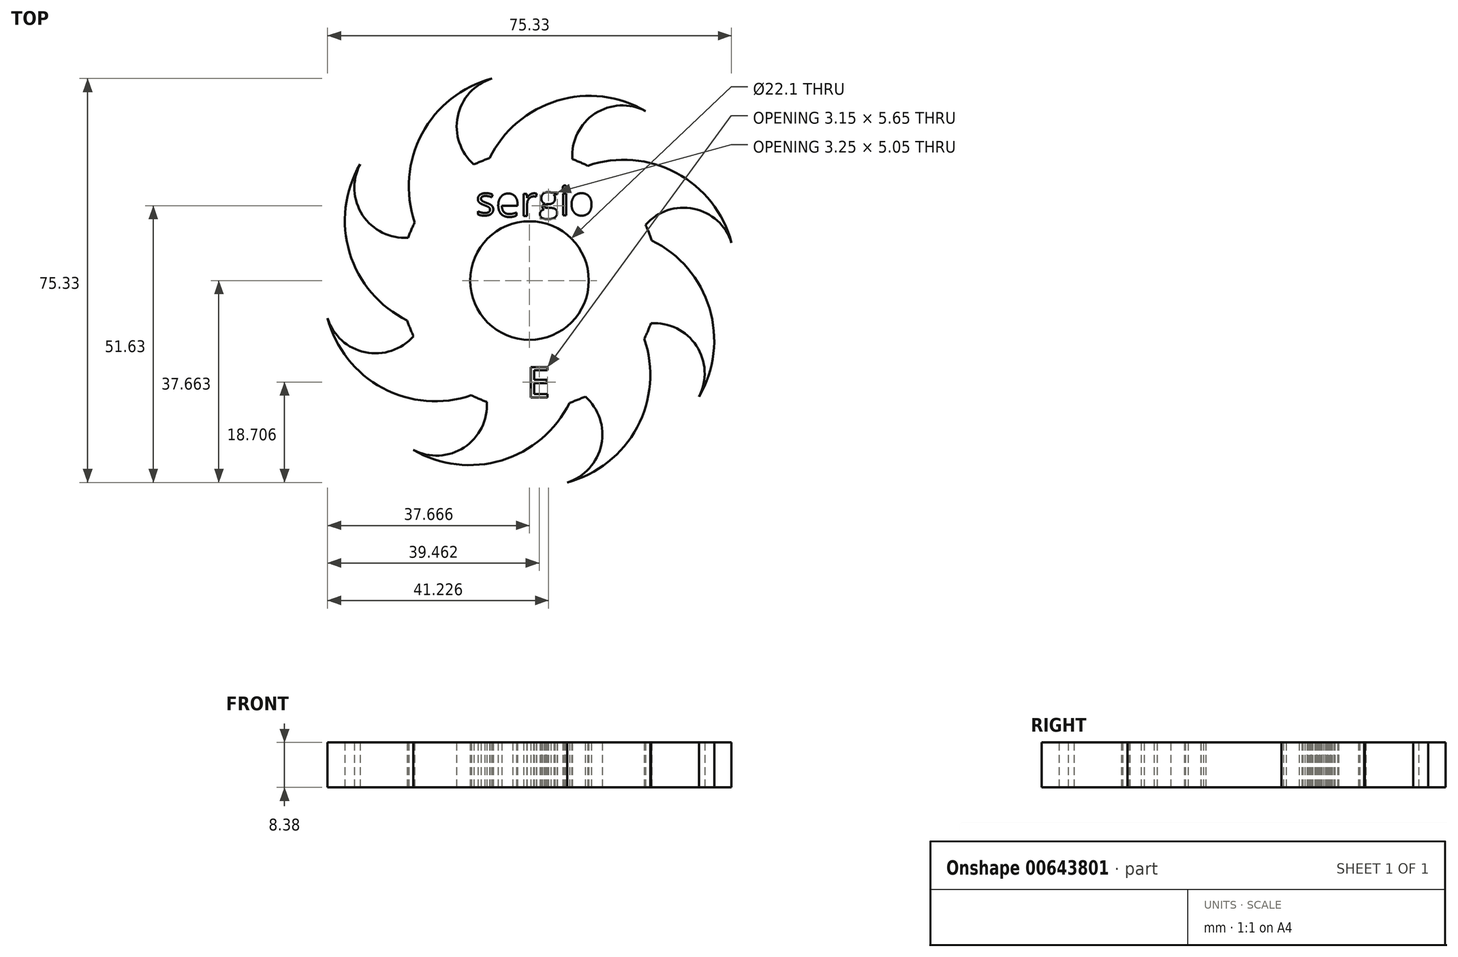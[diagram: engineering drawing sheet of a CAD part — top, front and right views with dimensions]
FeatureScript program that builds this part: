
annotation { "Feature Type Name" : "Feature", "Feature Type Description" : "" }
export const myFeature = defineFeature(function(context is Context, id is Id, definition is map)
    precondition{}
    {
        {
            var Q0;
            Q0=qCreatedBy(makeId("Top.planeOp"),FACE);
            var sketch = newSketch(context, id + "F0", { "sketchPlane" : qUnion([Q0])});
            skArc(sketch, "E0", {"start": v(-10.92, 50.97) * mm, "mid": v(-24.18, 40.22) * mm, "end": v(-24.92, 23.18) * mm});
            skArc(sketch, "E1", {"start": v(-10.92, 50.97) * mm, "mid": v(-17.27, 43.93) * mm, "end": v(-14.25, 34.94) * mm});
            skArc(sketch, "E2.1.0", {"start": v(-35.49, 34.96) * mm, "mid": v(-37.27, 18) * mm, "end": v(-25.74, 5.4) * mm});
            skArc(sketch, "E2.1.1", {"start": v(-35.49, 34.96) * mm, "mid": v(-35, 25.5) * mm, "end": v(-26.51, 21.28) * mm});
            skArc(sketch, "E2.2.0", {"start": v(-41.55, 6.27) * mm, "mid": v(-30.8, -6.99) * mm, "end": v(-13.76, -7.74) * mm});
            skArc(sketch, "E2.2.1", {"start": v(-41.55, 6.27) * mm, "mid": v(-34.5, -0.09) * mm, "end": v(-25.52, 2.94) * mm});
            skArc(sketch, "E2.3.0", {"start": v(-25.54, -18.3) * mm, "mid": v(-8.57, -20.08) * mm, "end": v(4.01, -8.55) * mm});
            skArc(sketch, "E2.3.1", {"start": v(-25.54, -18.3) * mm, "mid": v(-16.07, -17.82) * mm, "end": v(-11.86, -9.32) * mm});
            skArc(sketch, "E2.4.0", {"start": v(3.15, -24.36) * mm, "mid": v(16.4, -13.62) * mm, "end": v(17.15, 3.43) * mm});
            skArc(sketch, "E2.4.1", {"start": v(3.15, -24.36) * mm, "mid": v(9.5, -17.32) * mm, "end": v(6.48, -8.34) * mm});
            skArc(sketch, "E2.5.0", {"start": v(27.72, -8.36) * mm, "mid": v(29.5, 8.62) * mm, "end": v(17.97, 21.2) * mm});
            skArc(sketch, "E2.5.1", {"start": v(27.72, -8.36) * mm, "mid": v(27.24, 1.12) * mm, "end": v(18.74, 5.33) * mm});
            skArc(sketch, "E2.6.0", {"start": v(33.78, 20.34) * mm, "mid": v(23.04, 33.6) * mm, "end": v(5.99, 34.34) * mm});
            skArc(sketch, "E2.6.1", {"start": v(33.78, 20.34) * mm, "mid": v(26.74, 26.7) * mm, "end": v(17.75, 23.66) * mm});
            skArc(sketch, "E2.7.0", {"start": v(17.77, 44.9) * mm, "mid": v(0.8, 46.69) * mm, "end": v(-11.78, 35.16) * mm});
            skArc(sketch, "E2.7.1", {"start": v(17.77, 44.9) * mm, "mid": v(8.3, 44.43) * mm, "end": v(4.1, 35.93) * mm});
            skPoint(sketch, "E2.center", {"position": v(-3.88, 13.3) * mm});
            skArc(sketch, "E3", {"start": v(-11.34, 36.1) * mm, "mid": v(-12.81, 35.57) * mm, "end": v(-14.25, 34.94) * mm});
            skCircle(sketch, "E4", {"center": v(-3.88, 13.3) * mm, "radius": 11.05 * mm});
            skArc(sketch, "E5.trimOffspring", {"start": v(-25.28, 24.15) * mm, "mid": v(-25.94, 22.73) * mm, "end": v(-26.51, 21.28) * mm});
            skArc(sketch, "E6.trimOffspring", {"start": v(-26.69, 5.84) * mm, "mid": v(-26.15, 4.37) * mm, "end": v(-25.52, 2.94) * mm});
            skArc(sketch, "E7.trimOffspring", {"start": v(-14.73, -8.1) * mm, "mid": v(-13.32, -8.76) * mm, "end": v(-11.86, -9.32) * mm});
            skArc(sketch, "E8.trimOffspring", {"start": v(3.58, -9.5) * mm, "mid": v(5.05, -8.96) * mm, "end": v(6.48, -8.34) * mm});
            skArc(sketch, "E9.trimOffspring", {"start": v(17.51, 2.46) * mm, "mid": v(18.18, 3.87) * mm, "end": v(18.74, 5.33) * mm});
            skArc(sketch, "E10.trimOffspring", {"start": v(18.92, 20.76) * mm, "mid": v(18.38, 22.23) * mm, "end": v(17.75, 23.66) * mm});
            skArc(sketch, "E11.trimOffspring", {"start": v(6.96, 34.7) * mm, "mid": v(5.55, 35.36) * mm, "end": v(4.1, 35.93) * mm});
            skText(sketch, "E12", { "text": "s", "fontName": "OpenSans-Regular.ttf"});
            skText(sketch, "E13", { "text": "e", "fontName": "OpenSans-Regular.ttf"});
            skText(sketch, "E14", { "text": "r", "fontName": "OpenSans-Regular.ttf"});
            skText(sketch, "E15", { "text": "i", "fontName": "OpenSans-Regular.ttf"});
            skText(sketch, "E16", { "text": "o", "fontName": "OpenSans-Regular.ttf"});
            skText(sketch, "E17", { "text": "E", "fontName": "OpenSans-Regular.ttf"});
            skText(sketch, "E18", { "text": "g", "fontName": "OpenSans-Regular.ttf"});
            const initialGuessF0  = {"E12": [-0.01391, 0.02547, 1, 0, 0.00545], "E13": [-0.01016, 0.02522, 1, 0, 0.0057], "E14": [-0.00562, 0.02534, 1, 0, 0.00558], "E15": [0.00172, 0.02547, 1, 0, 0.00545], "E16": [0.00353, 0.02547, 1, 0, 0.00545], "E17": [-0.00444, -0.00848, 1, 0, 0.0057], "E18": [-0.00207, 0.02629, 1, 0, 0.00463]};
            skSetInitialGuess(sketch, initialGuessF0);
            skSolve(sketch);
        }
        {
            var Q0;
            {var subQ15=sQuery(id+"F0.wireOp",EDGE,"E1");Q0=makeQuery(id+"F0.imprint","IMPRINT",FACE,{"disambiguationData":[TD([[makeQuery(id+"F0.imprint","IMPRINT",EDGE,{"derivedFrom":subQ15}),-1.0]])]});}
            extrude(context, id + "F1", {"entities" : qUnion([Q0]), "depth" : 8.38 * mm, "offsetDistance" : 25.4 * mm});
        }
    });
